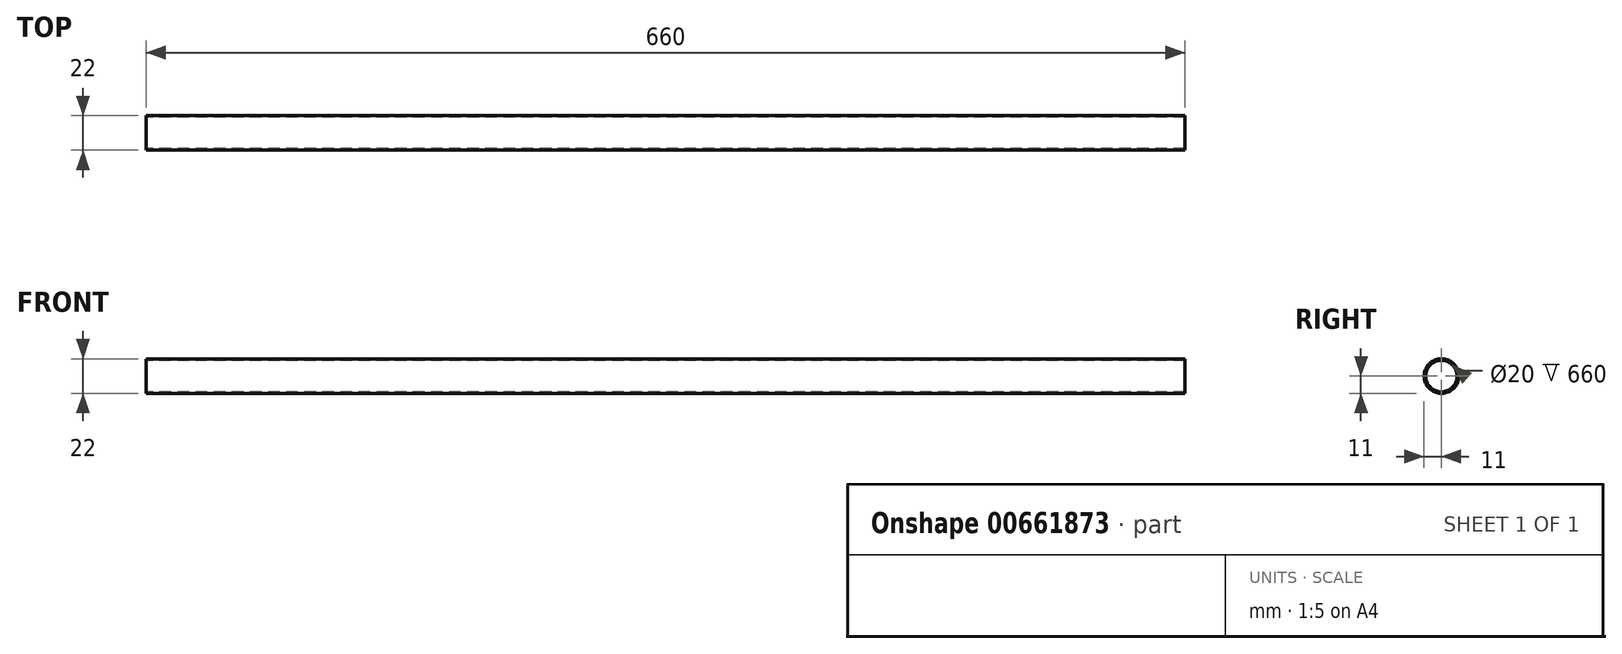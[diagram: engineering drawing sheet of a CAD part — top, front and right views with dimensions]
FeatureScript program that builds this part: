
annotation { "Feature Type Name" : "Feature", "Feature Type Description" : "" }
export const myFeature = defineFeature(function(context is Context, id is Id, definition is map)
    precondition{}
    {
        {
            var Q0;
            Q0=qCreatedBy(makeId("Right.planeOp"),FACE);
            var sketch = newSketch(context, id + "F0", { "sketchPlane" : qUnion([Q0])});
            skCircle(sketch, "E0", {"center": v(0, 0) * mm, "radius": 10 * mm});
            skCircle(sketch, "E1", {"center": v(0, 0) * mm, "radius": 11 * mm});
            skSolve(sketch);
        }
        {
            var Q0;
            Q0 = qSketchRegion(id + "F0", true);
            extrude(context, id + "F1", {"entities" : qUnion([Q0]), "depth" : 660 * mm, "offsetDistance" : 25 * mm, "symmetric" : true});
        }
    });
